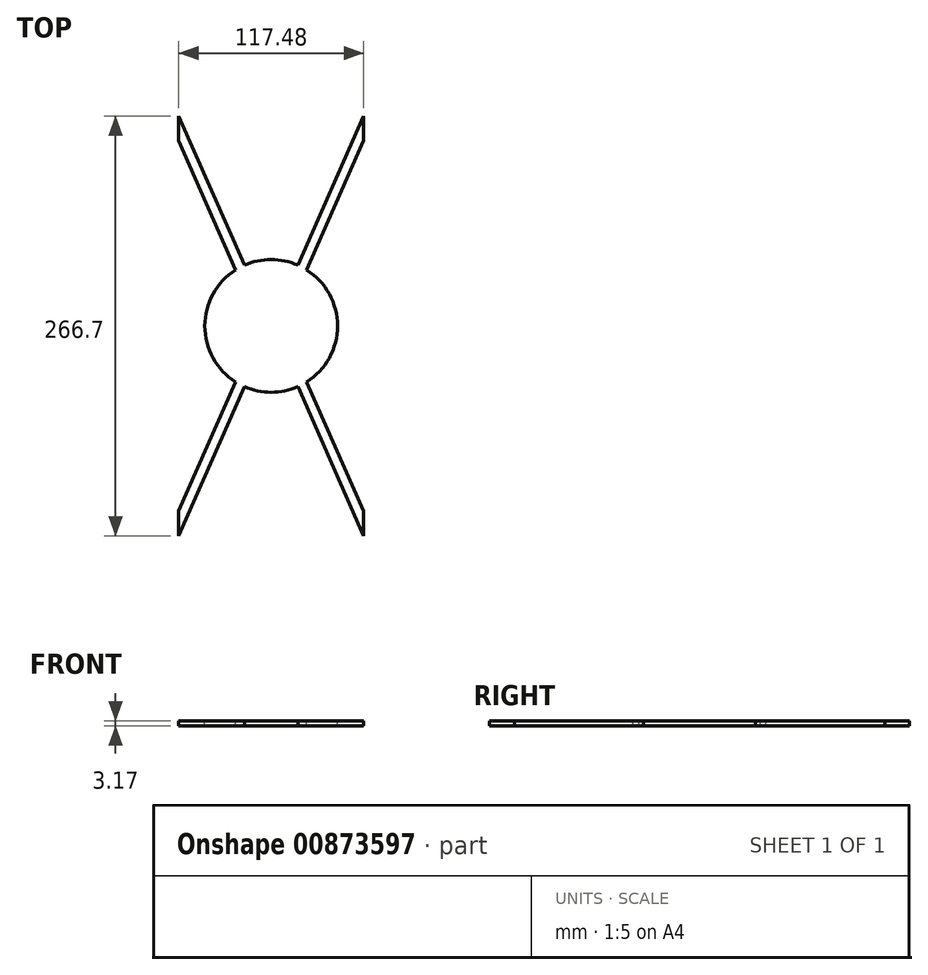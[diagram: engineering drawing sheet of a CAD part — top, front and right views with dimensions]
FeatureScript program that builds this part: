
annotation { "Feature Type Name" : "Feature", "Feature Type Description" : "" }
export const myFeature = defineFeature(function(context is Context, id is Id, definition is map)
    precondition{}
    {
        {
            var Q0;
            Q0=qCreatedBy(makeId("Top.planeOp"),FACE);
            var sketch = newSketch(context, id + "F0", { "sketchPlane" : qUnion([Q0])});
            skLineSegment(sketch, "E0.bottom", {"start": v(0, 0) * mm, "end": v(117.48, 0) * mm, "construction": true});
            skLineSegment(sketch, "E0.top", {"start": v(0, -266.7) * mm, "end": v(117.48, -266.7) * mm, "construction": true});
            skLineSegment(sketch, "E0.left", {"start": v(0, 0) * mm, "end": v(0, -266.7) * mm, "construction": true});
            skLineSegment(sketch, "E0.right", {"start": v(117.48, 0) * mm, "end": v(117.48, -266.7) * mm, "construction": true});
            skCircle(sketch, "E1", {"center": v(58.74, -133.35) * mm, "radius": 42.16 * mm});
            skPoint(sketch, "E1.centerSnap0", {"position": v(0, -133.35) * mm});
            skPoint(sketch, "E1.centerSnap1", {"position": v(58.74, 0) * mm});
            skLineSegment(sketch, "E2", {"start": v(117.48, 0) * mm, "end": v(75.73, -94.76) * mm});
            skLineSegment(sketch, "E3", {"start": v(0, 0) * mm, "end": v(41.74, -94.76) * mm});
            skLineSegment(sketch, "E4.0", {"start": v(117.48, -15.75) * mm, "end": v(81.35, -97.76) * mm});
            skLineSegment(sketch, "E4.1", {"start": v(0, -15.75) * mm, "end": v(36.12, -97.76) * mm});
            skLineSegment(sketch, "E5.trimOffspring", {"start": v(81.35, -168.94) * mm, "end": v(117.48, -250.95) * mm});
            skLineSegment(sketch, "E6.trimOffspring", {"start": v(75.73, -171.94) * mm, "end": v(117.48, -266.7) * mm});
            skLineSegment(sketch, "E7.trimOffspring", {"start": v(41.74, -171.94) * mm, "end": v(0, -266.7) * mm});
            skLineSegment(sketch, "E8.trimOffspring", {"start": v(36.12, -168.94) * mm, "end": v(0, -250.95) * mm});
            skLineSegment(sketch, "E9", {"start": v(0, 0) * mm, "end": v(0, -15.75) * mm});
            skLineSegment(sketch, "E10", {"start": v(117.48, 0) * mm, "end": v(117.48, -15.75) * mm});
            skLineSegment(sketch, "E11", {"start": v(117.48, -250.95) * mm, "end": v(117.48, -266.7) * mm});
            skLineSegment(sketch, "E12", {"start": v(0, -250.95) * mm, "end": v(0, -266.7) * mm});
            skSolve(sketch);
        }
        {
            var Q0;
            Q0 = qSketchRegion(id + "F0", true);
            extrude(context, id + "F1", {"entities" : qUnion([Q0]), "oppositeDirection" : true, "depth" : 3.17 * mm, "offsetDistance" : 25.4 * mm});
        }
    });
